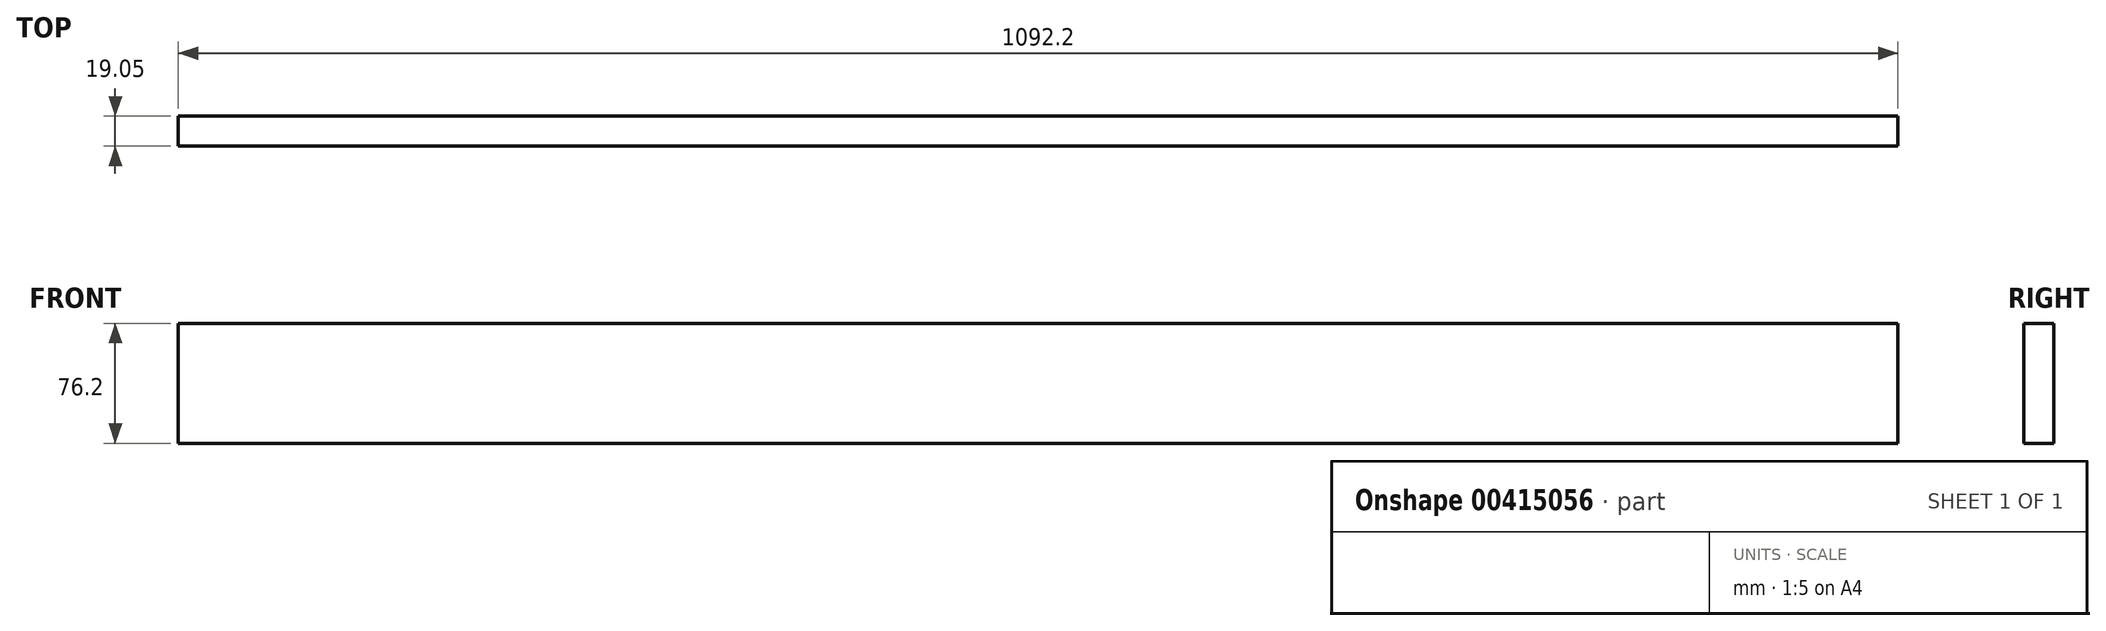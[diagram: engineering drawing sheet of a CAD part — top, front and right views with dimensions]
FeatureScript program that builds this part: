
annotation { "Feature Type Name" : "Feature", "Feature Type Description" : "" }
export const myFeature = defineFeature(function(context is Context, id is Id, definition is map)
    precondition{}
    {
        {
            var Q0;
            Q0=qCreatedBy(makeId("Front.planeOp"),FACE);
            var sketch = newSketch(context, id + "F0", { "sketchPlane" : qUnion([Q0])});
            skLineSegment(sketch, "E0.bottom", {"start": v(0, 0) * mm, "end": v(1092.2, 0) * mm});
            skLineSegment(sketch, "E0.top", {"start": v(0, 76.2) * mm, "end": v(1092.2, 76.2) * mm});
            skLineSegment(sketch, "E0.left", {"start": v(0, 0) * mm, "end": v(0, 76.2) * mm});
            skLineSegment(sketch, "E0.right", {"start": v(1092.2, 0) * mm, "end": v(1092.2, 76.2) * mm});
            skSolve(sketch);
        }
        {
            var Q0;
            Q0=makeQuery(id+"F0.imprint","IMPRINT",FACE,{"disambiguationData":[TD([[makeQuery(id+"F0.imprint","IMPRINT",EDGE,{"derivedFrom":sQuery(id+"F0.wireOp",EDGE,"E0.bottom")}),1.0]])]});
            extrude(context, id + "F1", {"entities" : qUnion([Q0]), "depth" : 19.05 * mm, "offsetDistance" : 25.4 * mm});
        }
    });
